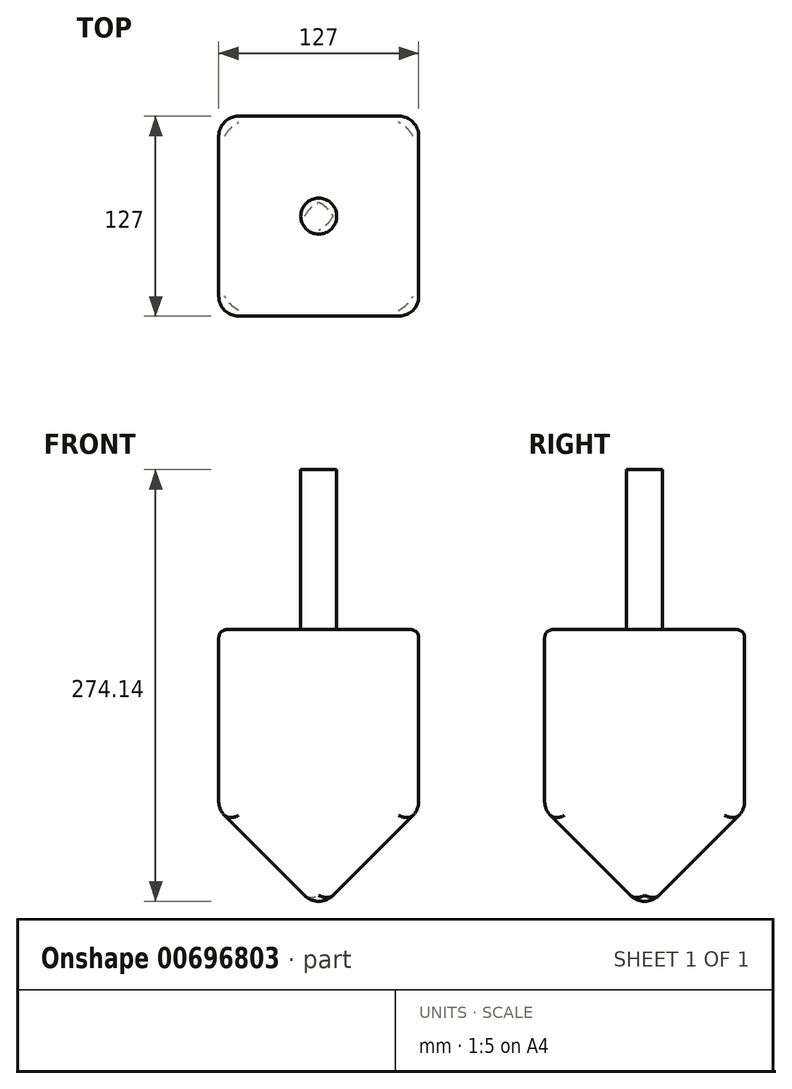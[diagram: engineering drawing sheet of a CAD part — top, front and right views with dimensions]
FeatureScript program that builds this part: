
annotation { "Feature Type Name" : "Feature", "Feature Type Description" : "" }
export const myFeature = defineFeature(function(context is Context, id is Id, definition is map)
    precondition{}
    {
        {
            var Q0;
            Q0=qCreatedBy(makeId("Top.planeOp"),FACE);
            var sketch = newSketch(context, id + "F0", { "sketchPlane" : qUnion([Q0])});
            skLineSegment(sketch, "E0.bottom", {"start": v(63.5, 63.5) * mm, "end": v(-63.5, 63.5) * mm});
            skLineSegment(sketch, "E0.top", {"start": v(63.5, -63.5) * mm, "end": v(-63.5, -63.5) * mm});
            skLineSegment(sketch, "E0.left", {"start": v(63.5, 63.5) * mm, "end": v(63.5, -63.5) * mm});
            skLineSegment(sketch, "E0.right", {"start": v(-63.5, 63.5) * mm, "end": v(-63.5, -63.5) * mm});
            skPoint(sketch, "E0.middle", {"position": v(0, 0) * mm});
            skSolve(sketch);
        }
        {
            var Q0;
            Q0=makeQuery(id+"F0.imprint","IMPRINT",FACE,{"disambiguationData":[TD([[makeQuery(id+"F0.imprint","IMPRINT",EDGE,{"derivedFrom":sQuery(id+"F0.wireOp",EDGE,"E0.bottom")}),1.0]])]});
            extrude(context, id + "F1", {"entities" : qUnion([Q0]), "depth" : 177.8 * mm, "offsetDistance" : 25.4 * mm});
        }
        {
            var Q0;
            Q0=makeQuery(id+"F1.opExtrude","CAP_FACE",FACE,{"disambiguationData":[OSD([sQuery(id+"F0.wireOp",EDGE,"E0.bottom"),sQuery(id+"F0.wireOp",EDGE,"E0.top"),sQuery(id+"F0.wireOp",EDGE,"E0.left"),sQuery(id+"F0.wireOp",EDGE,"E0.right")])],"isStart":true});
            chamfer(context, id + "F2", {"entities" : qUnion([Q0]), "width" : 63.5 * mm, "tangentPropagation" : true});
        }
        {
            var Q0;
            Q0=makeQuery(id+"F2.opChamfer","BLEND_EDGE",EDGE,{"blendedFrom":[makeQuery(id+"F1.opExtrude","CAP_EDGE",EDGE,{"disambiguationData":[OSD([sQuery(id+"F0.wireOp",EDGE,"E0.top")])],"isStart":true}),makeQuery(id+"F1.opExtrude","CAP_EDGE",EDGE,{"disambiguationData":[OSD([sQuery(id+"F0.wireOp",EDGE,"E0.right")])],"isStart":true})],"blendedInto":[]});
            var Q1;
            Q1=makeQuery(id+"F2.opChamfer","BLEND_EDGE",EDGE,{"blendedFrom":[makeQuery(id+"F1.opExtrude","CAP_EDGE",EDGE,{"disambiguationData":[OSD([sQuery(id+"F0.wireOp",EDGE,"E0.bottom")])],"isStart":true}),makeQuery(id+"F1.opExtrude","CAP_EDGE",EDGE,{"disambiguationData":[OSD([sQuery(id+"F0.wireOp",EDGE,"E0.right")])],"isStart":true})],"blendedInto":[]});
            var Q2;
            Q2=makeQuery(id+"F2.opChamfer","BLEND_EDGE",EDGE,{"blendedFrom":[makeQuery(id+"F1.opExtrude","CAP_EDGE",EDGE,{"disambiguationData":[OSD([sQuery(id+"F0.wireOp",EDGE,"E0.bottom")])],"isStart":true}),makeQuery(id+"F1.opExtrude","CAP_EDGE",EDGE,{"disambiguationData":[OSD([sQuery(id+"F0.wireOp",EDGE,"E0.left")])],"isStart":true})],"blendedInto":[]});
            var Q3;
            Q3=makeQuery(id+"F2.opChamfer","BLEND_EDGE",EDGE,{"blendedFrom":[makeQuery(id+"F1.opExtrude","CAP_EDGE",EDGE,{"disambiguationData":[OSD([sQuery(id+"F0.wireOp",EDGE,"E0.top")])],"isStart":true}),makeQuery(id+"F1.opExtrude","CAP_EDGE",EDGE,{"disambiguationData":[OSD([sQuery(id+"F0.wireOp",EDGE,"E0.left")])],"isStart":true})],"blendedInto":[]});
            fillet(context, id + "F3", {"entities" : qUnion([Q0, Q1, Q2, Q3]), "radius" : 12.7 * mm, "tangentPropagation" : true, "allowEdgeOverflow" : false});
        }
        {
            var Q0;
            Q0=makeQuery(id+"F1.opExtrude","SWEPT_EDGE",EDGE,{"disambiguationData":[OSD([sQuery(id+"F0.wireOp",EDGE,"E0.top"),sQuery(id+"F0.wireOp",EDGE,"E0.right")])]});
            var Q1;
            Q1=makeQuery(id+"F1.opExtrude","SWEPT_EDGE",EDGE,{"disambiguationData":[OSD([sQuery(id+"F0.wireOp",EDGE,"E0.bottom"),sQuery(id+"F0.wireOp",EDGE,"E0.right")])]});
            var Q2;
            Q2=makeQuery(id+"F1.opExtrude","SWEPT_EDGE",EDGE,{"disambiguationData":[OSD([sQuery(id+"F0.wireOp",EDGE,"E0.bottom"),sQuery(id+"F0.wireOp",EDGE,"E0.left")])]});
            var Q3;
            Q3=makeQuery(id+"F1.opExtrude","SWEPT_EDGE",EDGE,{"disambiguationData":[OSD([sQuery(id+"F0.wireOp",EDGE,"E0.top"),sQuery(id+"F0.wireOp",EDGE,"E0.left")])]});
            fillet(context, id + "F4", {"entities" : qUnion([Q0, Q1, Q2, Q3]), "radius" : 12.7 * mm, "tangentPropagation" : true, "allowEdgeOverflow" : false});
        }
        {
            var Q0;
            {var subQ0=sQuery(id+"F0.wireOp",EDGE,"E0.left");Q0=makeQuery(id+"F2.opChamfer","BLEND_EDGE",EDGE,{"blendedFrom":[makeQuery(id+"F1.opExtrude","CAP_EDGE",EDGE,{"disambiguationData":[OSD([subQ0])],"isStart":true}),makeQuery(id+"F1.opExtrude","SWEPT_FACE",FACE,{"disambiguationData":[OSD([subQ0])]})],"blendedInto":[makeQuery(id+"F1.opExtrude","SWEPT_FACE",FACE,{"disambiguationData":[OSD([subQ0])]})]});}
            var Q1;
            {var subQ0=sQuery(id+"F0.wireOp",EDGE,"E0.top");Q1=makeQuery(id+"F2.opChamfer","BLEND_EDGE",EDGE,{"blendedFrom":[makeQuery(id+"F1.opExtrude","CAP_EDGE",EDGE,{"disambiguationData":[OSD([subQ0])],"isStart":true}),makeQuery(id+"F1.opExtrude","SWEPT_FACE",FACE,{"disambiguationData":[OSD([subQ0])]})],"blendedInto":[makeQuery(id+"F1.opExtrude","SWEPT_FACE",FACE,{"disambiguationData":[OSD([subQ0])]})]});}
            var Q2;
            {var subQ0=sQuery(id+"F0.wireOp",EDGE,"E0.right");Q2=makeQuery(id+"F2.opChamfer","BLEND_EDGE",EDGE,{"blendedFrom":[makeQuery(id+"F1.opExtrude","CAP_EDGE",EDGE,{"disambiguationData":[OSD([subQ0])],"isStart":true}),makeQuery(id+"F1.opExtrude","SWEPT_FACE",FACE,{"disambiguationData":[OSD([subQ0])]})],"blendedInto":[makeQuery(id+"F1.opExtrude","SWEPT_FACE",FACE,{"disambiguationData":[OSD([subQ0])]})]});}
            var Q3;
            {var subQ0=sQuery(id+"F0.wireOp",EDGE,"E0.bottom");Q3=makeQuery(id+"F2.opChamfer","BLEND_EDGE",EDGE,{"blendedFrom":[makeQuery(id+"F1.opExtrude","CAP_EDGE",EDGE,{"disambiguationData":[OSD([subQ0])],"isStart":true}),makeQuery(id+"F1.opExtrude","SWEPT_FACE",FACE,{"disambiguationData":[OSD([subQ0])]})],"blendedInto":[makeQuery(id+"F1.opExtrude","SWEPT_FACE",FACE,{"disambiguationData":[OSD([subQ0])]})]});}
            fillet(context, id + "F5", {"entities" : qUnion([Q0, Q1, Q2, Q3]), "radius" : 12.7 * mm, "tangentPropagation" : true, "allowEdgeOverflow" : false});
        }
        {
            var Q0;
            Q0=makeQuery(id+"F1.opExtrude","CAP_FACE",FACE,{"disambiguationData":[OSD([sQuery(id+"F0.wireOp",EDGE,"E0.bottom"),sQuery(id+"F0.wireOp",EDGE,"E0.top"),sQuery(id+"F0.wireOp",EDGE,"E0.left"),sQuery(id+"F0.wireOp",EDGE,"E0.right")])],"isStart":false});
            var sketch = newSketch(context, id + "F6", { "sketchPlane" : qUnion([Q0])});
            skCircle(sketch, "E1", {"center": v(0, 0) * mm, "radius": 11.43 * mm});
            skSolve(sketch);
        }
        {
            var Q0;
            Q0=makeQuery(id+"F6.imprint","IMPRINT",FACE,{"disambiguationData":[TD([[makeQuery(id+"F6.imprint","IMPRINT",EDGE,{"derivedFrom":sQuery(id+"F6.wireOp",EDGE,"E1")}),1.0]])]});
            extrude(context, id + "F7", {"entities" : qUnion([Q0]), "operationType" : NewBodyOperationType.ADD, "depth" : 101.6 * mm, "offsetDistance" : 25.4 * mm});
        }
        {
            var Q0;
            Q0=makeQuery(id+"F1.opExtrude","CAP_EDGE",EDGE,{"disambiguationData":[OSD([sQuery(id+"F0.wireOp",EDGE,"E0.left")])],"isStart":false});
            fillet(context, id + "F8", {"entities" : qUnion([Q0]), "radius" : 5.08 * mm, "tangentPropagation" : true, "allowEdgeOverflow" : false});
        }
    });
